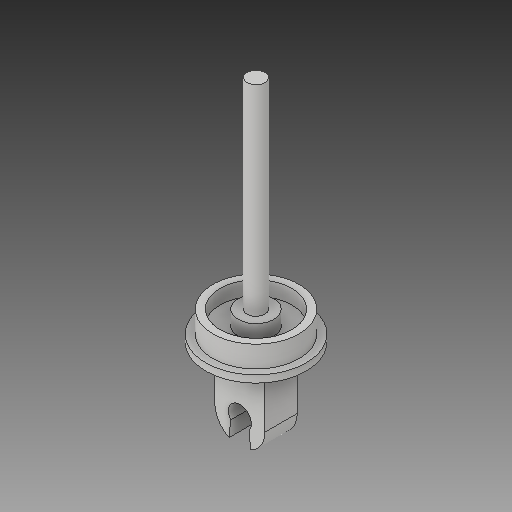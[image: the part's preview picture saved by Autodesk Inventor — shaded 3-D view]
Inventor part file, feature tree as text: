
AUTODESK INVENTOR PART (.ipt)
format: ipt  version: 2019 (Build 230136000, 136)  size: 169,472 bytes
history: native  units: in
note: dims shown in document units (in); Inventor stores cm internally (conversion verified against a paired STEP export)
features: sketch x5, extrude x4, revolve x1
ambient origin geometry x8: Origin, YZ Plane, XZ Plane, XY Plane, X Axis, Y Axis, Z Axis, Center Point
bodies: Solid1 (feature_tree)
feature tree (10):
  extrude  "Extrusion1"  Depth=0.35in
  extrude  "Extrusion2"  Depth=0.16in
  revolve  "Revolution1"  [1 undecoded]
  extrude  "Extrusion3"  Depth=0.35in
  extrude  "Extrusion4"  Depth=0.15in
  sketch  "Sketch1"  dims[d0=0.35in d1=0.35in]
  sketch  "Sketch2"  dims[d2=0.225in d3=0.0in d4=0.16in]
  sketch  "Sketch3"  dims[d5=0.15in d6=0.13in]
  sketch  "Sketch4"  dims[d7=0.225in d8=0.0in d9=0.35in]
  sketch  "Sketch5"  dims[d10=0.25in d11=0.15in d12=0.05in d13=0.05in d14=90.0deg d15=0.25in d16=0.05in d17=0.1in d18=0.0in d19=0.125in d20=1.4in d21=0.0in]
note: 1 required parameter value undecoded (feature->parameter linkage not recoverable at this tier; creation-order binding heuristic only, values carry confidence <= 0.55)
